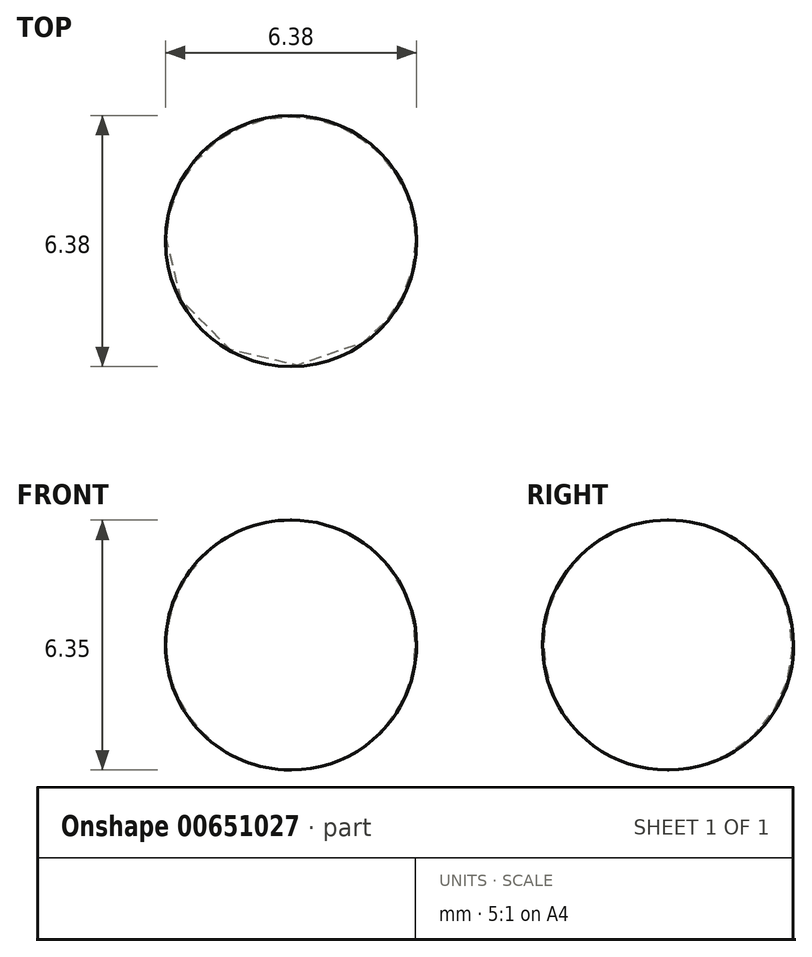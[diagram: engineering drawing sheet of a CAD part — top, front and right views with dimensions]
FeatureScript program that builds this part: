
annotation { "Feature Type Name" : "Feature", "Feature Type Description" : "" }
export const myFeature = defineFeature(function(context is Context, id is Id, definition is map)
    precondition{}
    {
        {
            var Q0;
            Q0=qCreatedBy(makeId("Front.planeOp"),FACE);
            var sketch = newSketch(context, id + "F0", { "sketchPlane" : qUnion([Q0])});
            skLineSegment(sketch, "E0", {"start": v(0, 0) * mm, "end": v(0, 6.35) * mm});
            skArc(sketch, "E1", {"start": v(0, 0) * mm, "mid": v(3.19, 3.17) * mm, "end": v(0, 6.35) * mm});
            skSolve(sketch);
        }
        {
            var Q0;
            Q0=makeQuery(id+"F0.imprint","IMPRINT",FACE,{"disambiguationData":[TD([[makeQuery(id+"F0.imprint","IMPRINT",EDGE,{"derivedFrom":sQuery(id+"F0.wireOp",EDGE,"E0")}),-1.0]])]});
            var Q1;
            Q1=sQuery(id+"F0.wireOp",EDGE,"E0");
            revolve(context, id + "F1", {"entities" : qUnion([Q0]), "axis" : qUnion([Q1]), "revolveType" : RevolveType.FULL});
        }
    });
